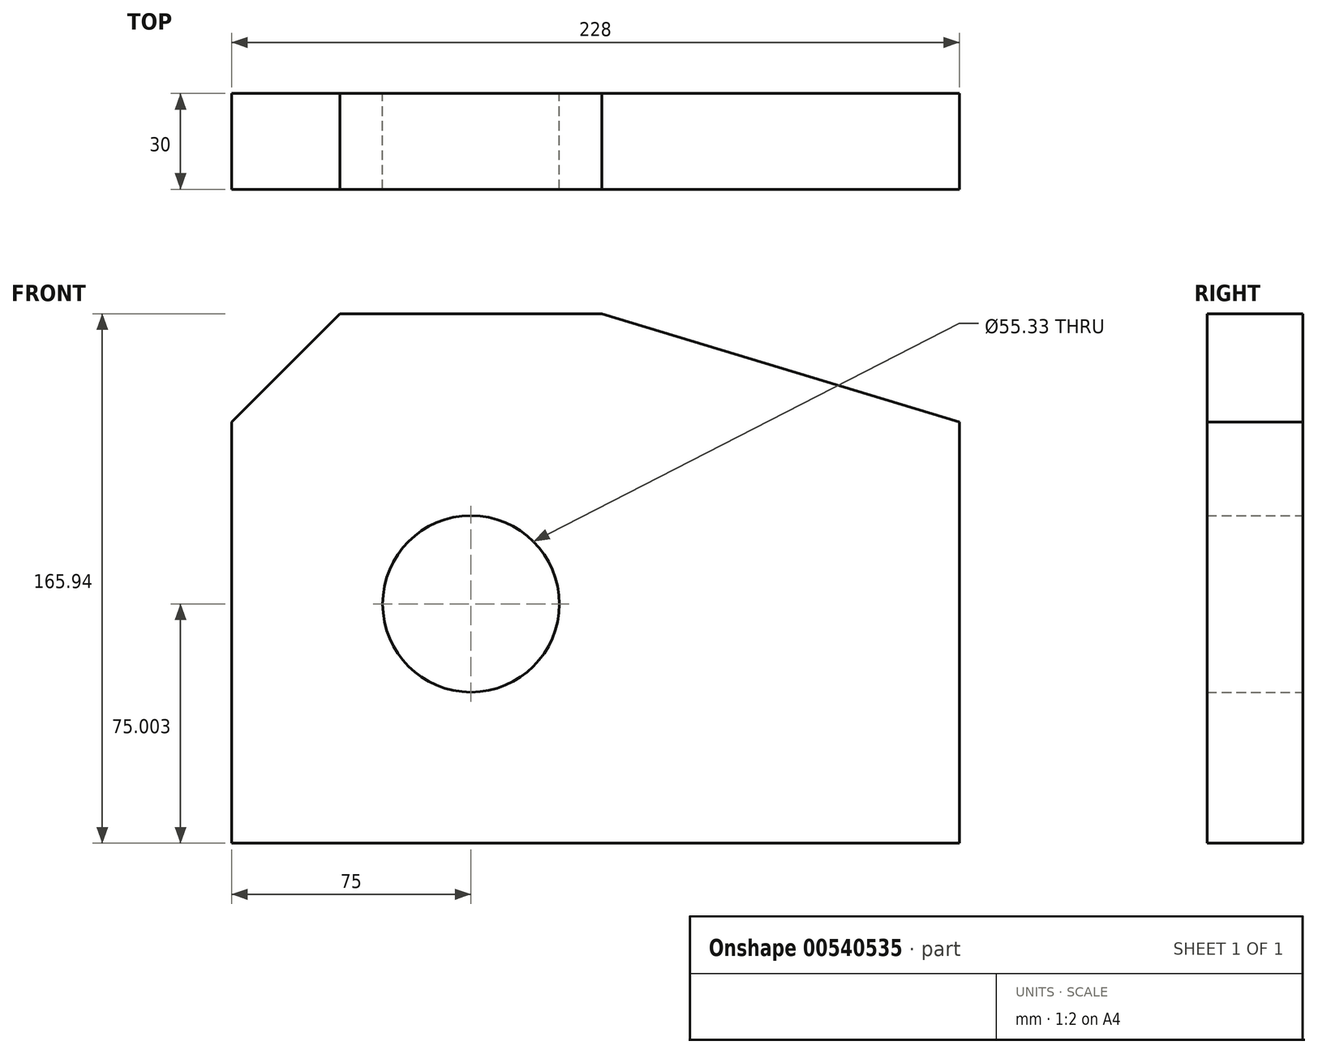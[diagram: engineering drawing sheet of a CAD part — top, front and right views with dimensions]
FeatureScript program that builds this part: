
annotation { "Feature Type Name" : "Feature", "Feature Type Description" : "" }
export const myFeature = defineFeature(function(context is Context, id is Id, definition is map)
    precondition{}
    {
        {
            var Q0;
            Q0=qCreatedBy(makeId("Front.planeOp"),FACE);
            var sketch = newSketch(context, id + "F0", { "sketchPlane" : qUnion([Q0])});
            skLineSegment(sketch, "E0", {"start": v(-81.4, 51.5) * mm, "end": v(-81.4, -80.5) * mm});
            skLineSegment(sketch, "E1", {"start": v(-81.4, -80.5) * mm, "end": v(146.6, -80.5) * mm});
            skLineSegment(sketch, "E2", {"start": v(-81.4, 51.5) * mm, "end": v(-47.46, 85.44) * mm});
            skLineSegment(sketch, "E3", {"start": v(-47.46, 85.44) * mm, "end": v(34.63, 85.44) * mm});
            skLineSegment(sketch, "E4", {"start": v(146.6, -80.5) * mm, "end": v(146.6, 51.5) * mm});
            skLineSegment(sketch, "E5", {"start": v(146.6, 51.5) * mm, "end": v(34.63, 85.44) * mm});
            skCircle(sketch, "E6", {"center": v(-6.4, -5.5) * mm, "radius": 27.67 * mm});
            skSolve(sketch);
        }
        {
            var Q0;
            Q0 = qSketchRegion(id + "F0", true);
            extrude(context, id + "F1", {"entities" : qUnion([Q0]), "depth" : 30 * mm, "offsetDistance" : 25 * mm});
        }
    });
